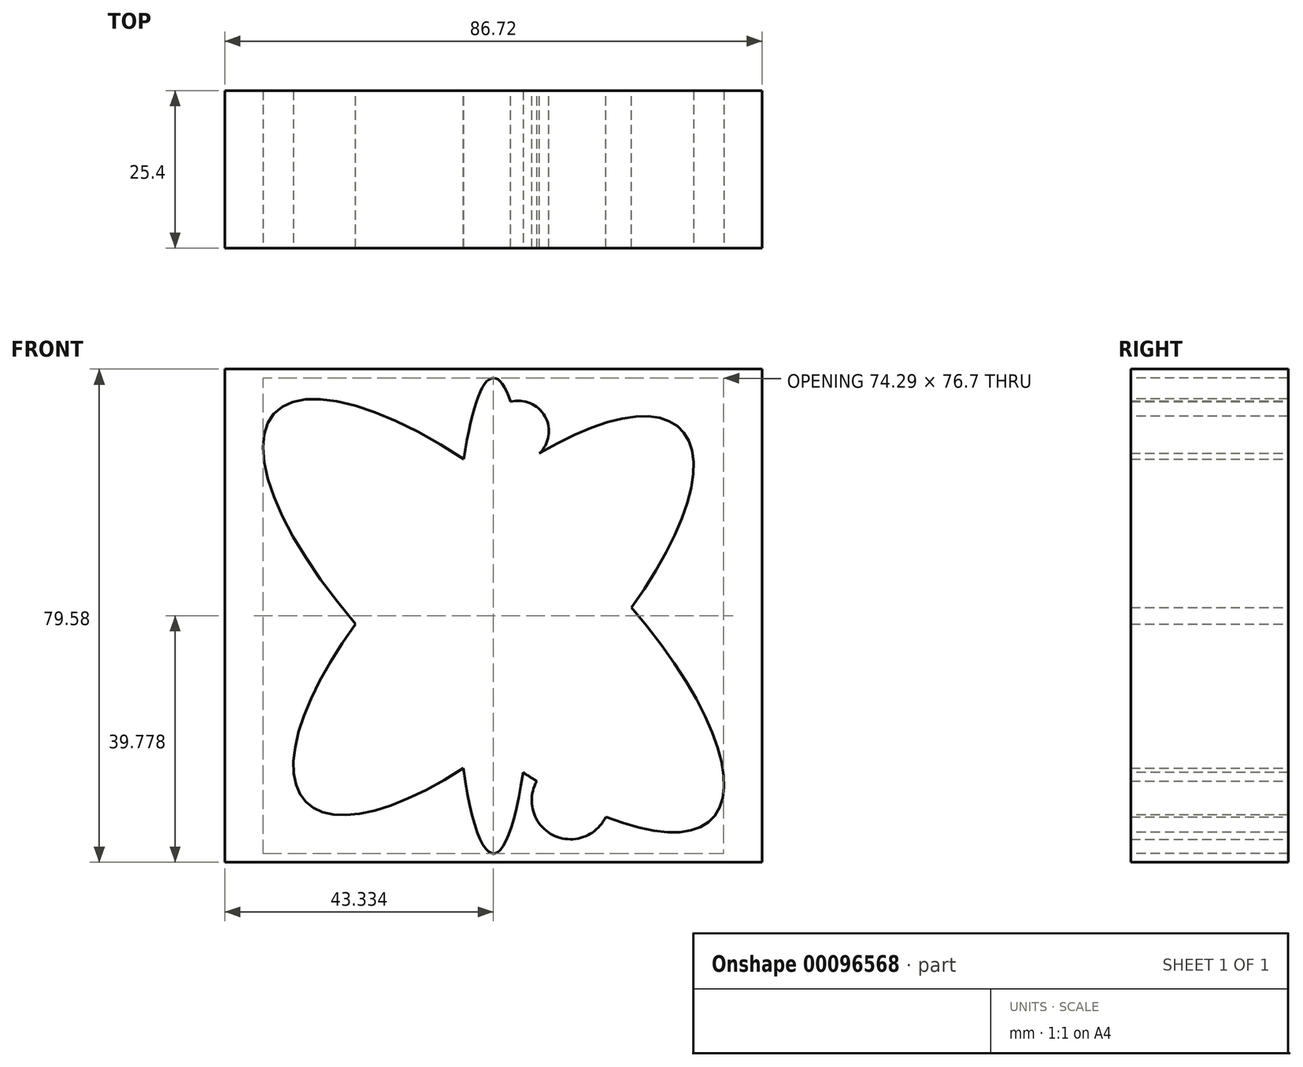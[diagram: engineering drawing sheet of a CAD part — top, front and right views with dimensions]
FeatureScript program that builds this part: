
annotation { "Feature Type Name" : "Feature", "Feature Type Description" : "" }
export const myFeature = defineFeature(function(context is Context, id is Id, definition is map)
    precondition{}
    {
        {
            var Q0;
            Q0=qCreatedBy(makeId("Front.planeOp"),FACE);
            var sketch = newSketch(context, id + "F0", { "sketchPlane" : qUnion([Q0])});
            skLineSegment(sketch, "E0.bottom", {"start": v(-43.36, 39.8) * mm, "end": v(43.36, 39.8) * mm});
            skLineSegment(sketch, "E0.top", {"start": v(-43.36, -39.8) * mm, "end": v(43.36, -39.8) * mm});
            skLineSegment(sketch, "E0.left", {"start": v(-43.36, 39.8) * mm, "end": v(-43.36, -39.8) * mm});
            skLineSegment(sketch, "E0.right", {"start": v(43.36, 39.8) * mm, "end": v(43.36, -39.8) * mm});
            skPoint(sketch, "E0.middle", {"position": v(0, 0) * mm});
            skEllipse(sketch, "E1", {"center": v(0, 0) * mm, "majorRadius": 48.14 * mm, "minorRadius": 16.98 * mm, "majorAxis": v(-0.73, 0.68)});
            skEllipse(sketch, "E2", {"center": v(0, 0) * mm, "majorRadius": 42.66 * mm, "minorRadius": 16.04 * mm, "majorAxis": v(0.7, 0.7)});
            skEllipse(sketch, "E3", {"center": v(0, 0) * mm, "majorRadius": 38.36 * mm, "minorRadius": 6.34 * mm, "majorAxis": v(0, 1)});
            skCircle(sketch, "E4", {"center": v(-13.96, 8.64) * mm, "radius": 5.63 * mm});
            skCircle(sketch, "E5", {"center": v(12.43, -29.8) * mm, "radius": 6.27 * mm});
            skCircle(sketch, "E6", {"center": v(4, 29.75) * mm, "radius": 4.93 * mm});
            skSolve(sketch);
        }
        {
            var Q0;
            Q0 = qSketchRegion(id + "F0", true);
            extrude(context, id + "F1", {"entities" : qUnion([Q0]), "depth" : 25.4 * mm});
        }
    });
